# Revit family: ERA_LF_PR_SPP-502
name_source: partatom
category: Осветительные приборы
units: mm (PartAtom-declared; Revit-internal decimal feet)

## family parameters
Всегда вертикально = Да
Заголовок OmniClass = Lighting
Источник света = Нет
На основе рабочей плоскости = Нет
Номер OmniClass = 23.80.70.00
Общий = Нет
При загрузке вырезать с полостями = Нет
Размер круглого соединителя = Использовать диаметр
Тип детали = Нормальный
Точка расчета площади = Да

## types (1)
- ERA_LF_PR_SPP-502
    ADSK_Единица измерения = шт.
    ADSK_Завод-изготовитель = ЭРА
    ADSK_Классификация нагрузок = Освещение
    ADSK_Количество фаз = 1
    ADSK_Коэффициент мощности = 0.9
    ADSK_Марка = SPP-502-0-50K-080
    ADSK_Масса = 1.42
    ADSK_Наименование = Светильник, LED, прямоугольный, уличный, IP65, 450х160х50 мм (ДхШхВ), 80 Вт, 5000 К, 8000 лм, класс защиты I, в комплекте (импульсный ac/dc драйвер с гальванической развязкой)
    ADSK_Наименование краткое = Светильник
    ADSK_Напряжение = 230 В
    ADSK_Номинальная мощность = 80 Вт
    ADSK_Обозначение = SPP-502-0-50K-080
    ADSK_Полная мощность = 89 В·А
    ADSK_Примечание = Импульсный AC/DC драйвер с гальванической развязкой, рассиватель поликарбонат
    ADSK_Размер_Высота = 50 мм
    ADSK_Размер_Диаметр = 0 мм
    ADSK_Размер_Длина = 450 мм
    ADSK_Размер_Ширина = 160 мм
    URL = https://www.eraworld.ru
    _Корпус_Высота = 50 мм
    _Корпус_Диаметр = 1 мм
    _Корпус_Длина = 450 мм
    _Корпус_Центр = 225 мм
    _Корпус_Ширина = 160 мм
    _УГО_Диаметр = 4.5 мм
    _УГО_Длина = 4.5 мм
    _УГО_Ширина = 1.6 мм
    Вспомогательные элементы = Нет
    Геометрия изделия = Прямоугольный
    ИС = LF_ИС_Пр_SPP-502 : SPP-502-0-50K-080
    Источник света = LED
    Класс защиты = I
    Класс пожароопасности = Нет
    Комплект = Импульсный AC/DC драйвер с гальванической развязкой
    Разработчик модели = https://www.teslabim.ru
    Степень защиты IP = IP65
    Тип установки = Уличный
    УГО_Масштаб = 100
    Цвет = Чёрный
